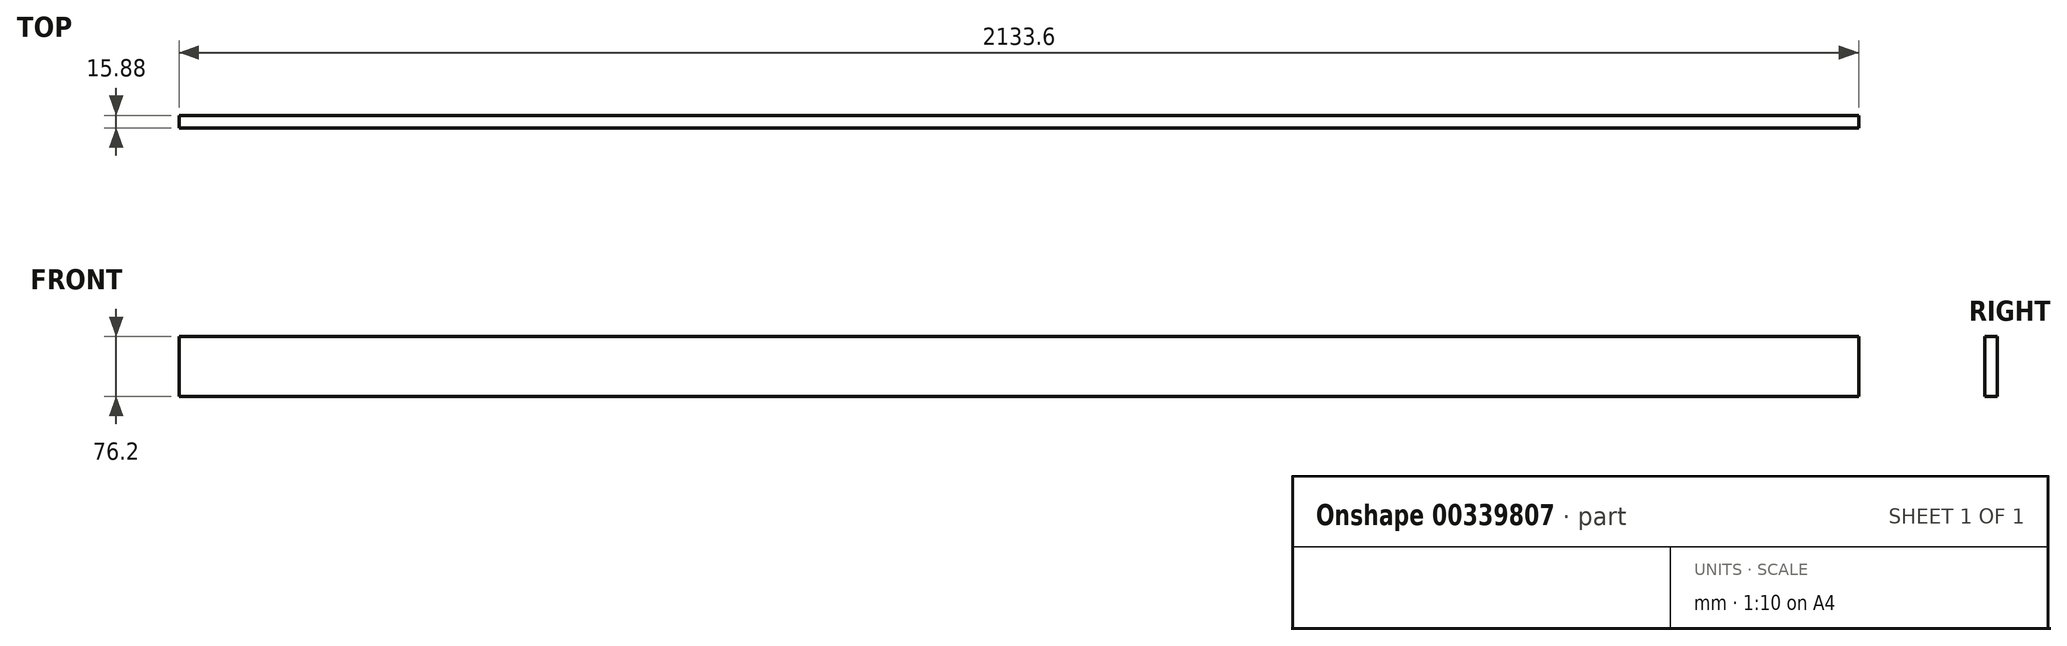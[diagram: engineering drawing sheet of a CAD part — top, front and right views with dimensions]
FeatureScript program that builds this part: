
annotation { "Feature Type Name" : "Feature", "Feature Type Description" : "" }
export const myFeature = defineFeature(function(context is Context, id is Id, definition is map)
    precondition{}
    {
        {
            var Q0;
            Q0=qCreatedBy(makeId("Front.planeOp"),FACE);
            var sketch = newSketch(context, id + "F0", { "sketchPlane" : qUnion([Q0])});
            skLineSegment(sketch, "E0.bottom", {"start": v(-86.82, 64.31) * mm, "end": v(2046.78, 64.31) * mm});
            skLineSegment(sketch, "E0.top", {"start": v(-86.82, -11.89) * mm, "end": v(2046.78, -11.89) * mm});
            skLineSegment(sketch, "E0.left", {"start": v(-86.82, 64.31) * mm, "end": v(-86.82, -11.89) * mm});
            skLineSegment(sketch, "E0.right", {"start": v(2046.78, 64.31) * mm, "end": v(2046.78, -11.89) * mm});
            skSolve(sketch);
        }
        {
            var Q0;
            Q0=makeQuery(id+"F0.imprint","IMPRINT",FACE,{"disambiguationData":[TD([[makeQuery(id+"F0.imprint","IMPRINT",EDGE,{"derivedFrom":sQuery(id+"F0.wireOp",EDGE,"E0.bottom")}),-1.0]])]});
            extrude(context, id + "F1", {"entities" : qUnion([Q0]), "oppositeDirection" : true, "depth" : 15.88 * mm});
        }
    });
